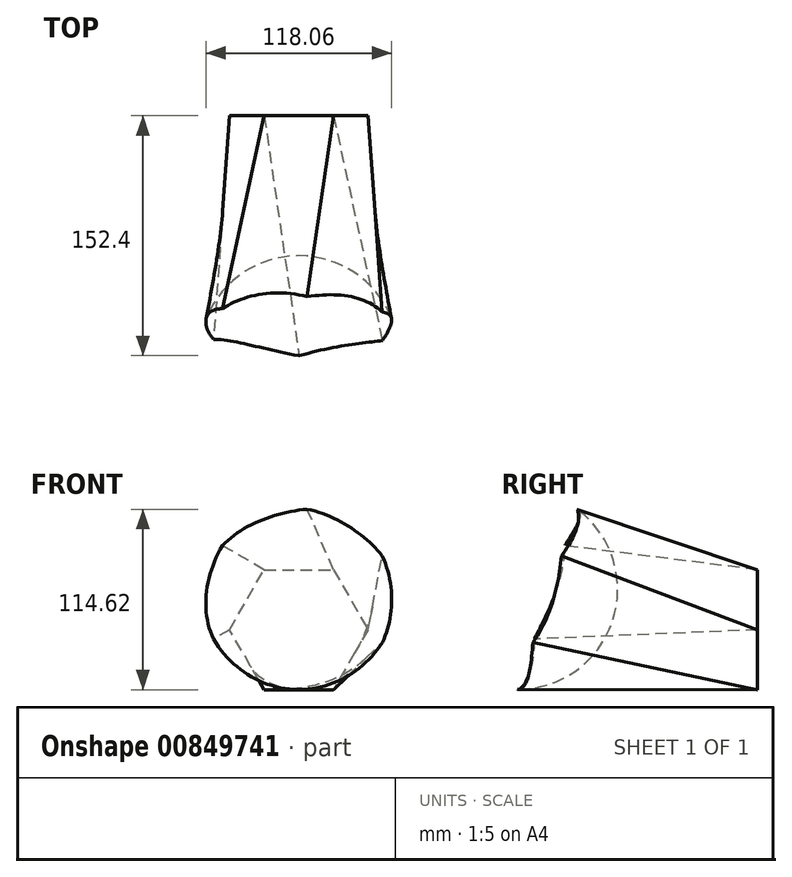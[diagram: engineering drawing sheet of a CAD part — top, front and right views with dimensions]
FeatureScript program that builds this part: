
annotation { "Feature Type Name" : "Feature", "Feature Type Description" : "" }
export const myFeature = defineFeature(function(context is Context, id is Id, definition is map)
    precondition{}
    {
        {
            var Q0;
            Q0=qCreatedBy(makeId("Front.planeOp"),FACE);
            var sketch = newSketch(context, id + "F0", { "sketchPlane" : qUnion([Q0])});
            skArc(sketch, "E0", {"start": v(0, -63.5) * mm, "mid": v(63.5, 0) * mm, "end": v(0, 63.5) * mm});
            skLineSegment(sketch, "E1", {"start": v(0, 63.5) * mm, "end": v(0, -63.5) * mm});
            skSolve(sketch);
        }
        {
            var Q0;
            Q0=qCreatedBy(makeId("Front.planeOp"),FACE);
            var sketch = newSketch(context, id + "F1", { "sketchPlane" : qUnion([Q0])});
            skLineSegment(sketch, "E2", {"start": v(0, 0) * mm, "end": v(0, 106.21) * mm});
            skSolve(sketch);
        }
        {
            var Q0;
            Q0=makeQuery(id+"F0.imprint","IMPRINT",FACE,{"disambiguationData":[TD([[makeQuery(id+"F0.imprint","IMPRINT",EDGE,{"derivedFrom":sQuery(id+"F0.wireOp",EDGE,"E0")}),1.0]])]});
            var Q1;
            Q1=sQuery(id+"F1.wireOp",EDGE,"E2");
            revolve(context, id + "F2", {"surfaceOperationType" : NewSurfaceOperationType.NEW, "entities" : qUnion([Q0]), "axis" : qUnion([Q1]), "revolveType" : RevolveType.FULL});
        }
        {
            var Q0;
            Q0=qCreatedBy(makeId("Front.planeOp"),FACE);
            var sketch = newSketch(context, id + "F3", { "sketchPlane" : qUnion([Q0])});
            skCircle(sketch, "E3", {"center": v(0, 0) * mm, "radius": 63.5 * mm});
            skSolve(sketch);
        }
        {
            var Q0;
            Q0=qCreatedBy(makeId("Front.planeOp"),FACE);
            cPlane(context, id + "F4", {"entities" : qUnion([Q0]), "cplaneType" : CPlaneType.OFFSET, "offset" : 152.4 * mm, "oppositeDirection" : true, "width" : 152.4 * mm, "height" : 152.4 * mm});
        }
        {
            var Q0;
            Q0=qCreatedBy(id+"F4.planeOp",FACE);
            var sketch = newSketch(context, id + "F5", { "sketchPlane" : qUnion([Q0])});
            skCircle(sketch, "E4.cCircle", {"center": v(0, -25.58) * mm, "radius": 38.1 * mm, "construction": true});
            skLineSegment(sketch, "E4.0", {"start": v(-44, -25.58) * mm, "end": v(-22, 12.52) * mm});
            skLineSegment(sketch, "E4.1", {"start": v(-22, 12.52) * mm, "end": v(22, 12.52) * mm});
            skLineSegment(sketch, "E4.2", {"start": v(22, 12.52) * mm, "end": v(44, -25.58) * mm});
            skLineSegment(sketch, "E4.3", {"start": v(44, -25.58) * mm, "end": v(22, -63.68) * mm});
            skLineSegment(sketch, "E4.4", {"start": v(22, -63.68) * mm, "end": v(-22, -63.68) * mm});
            skLineSegment(sketch, "E4.5", {"start": v(-22, -63.68) * mm, "end": v(-44, -25.58) * mm});
            skPoint(sketch, "E4.0.midPoint", {"position": v(-33, -6.53) * mm});
            skSolve(sketch);
        }
        {
            var Q1;
            Q1 = qSketchRegion(id + "F5", true);
            var Q2;
            Q2 = qSketchRegion(id + "F3", true);
            loft(context, id + "F6", {"operationType" : NewBodyOperationType.ADD, "sheetProfilesArray" : [{ "sheetProfileEntities" : qUnion([Q1]) }, { "sheetProfileEntities" : qUnion([Q2]) }]});
        }
    });
